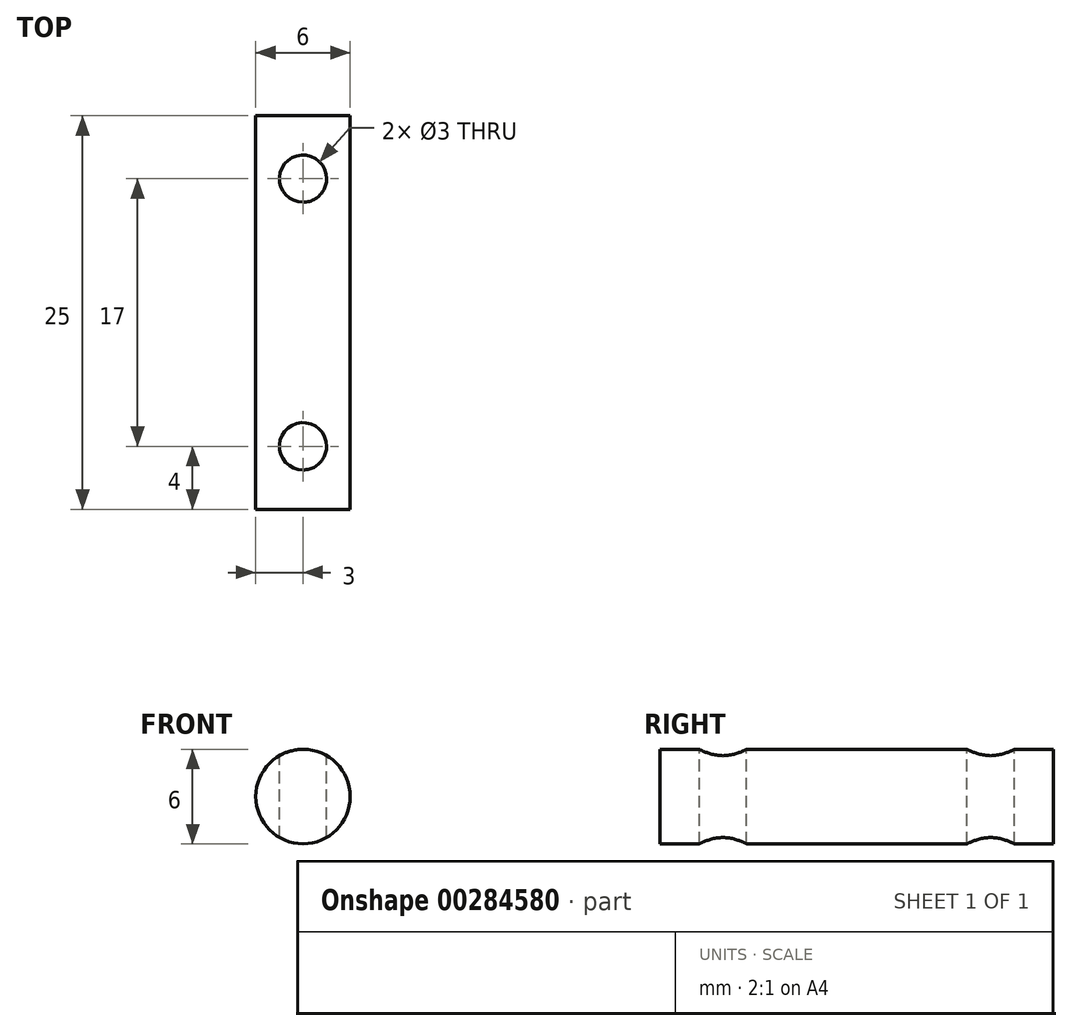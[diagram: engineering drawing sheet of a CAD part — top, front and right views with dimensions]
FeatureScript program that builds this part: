
annotation { "Feature Type Name" : "Feature", "Feature Type Description" : "" }
export const myFeature = defineFeature(function(context is Context, id is Id, definition is map)
    precondition{}
    {
        {
            var Q0;
            Q0=qCreatedBy(makeId("Front.planeOp"),FACE);
            var sketch = newSketch(context, id + "F0", { "sketchPlane" : qUnion([Q0])});
            skCircle(sketch, "E0", {"center": v(0, 0) * mm, "radius": 3 * mm});
            skSolve(sketch);
        }
        {
            var Q0;
            Q0=makeQuery(id+"F0.imprint","IMPRINT",FACE,{"disambiguationData":[TD([[makeQuery(id+"F0.imprint","IMPRINT",EDGE,{"derivedFrom":sQuery(id+"F0.wireOp",EDGE,"E0")}),1.0]])]});
            extrude(context, id + "F1", {"entities" : qUnion([Q0]), "depth" : 25 * mm});
        }
        {
            var Q0;
            Q0=qCreatedBy(makeId("Top.planeOp"),FACE);
            var sketch = newSketch(context, id + "F2", { "sketchPlane" : qUnion([Q0])});
            skPoint(sketch, "E1", {"position": v(0, -21) * mm});
            skPoint(sketch, "E2", {"position": v(0, -4) * mm});
            skPoint(sketch, "E3.start.orphan", {"position": v(0, 0) * mm});
            skCircle(sketch, "E4", {"center": v(0, -4) * mm, "radius": 1.5 * mm});
            skCircle(sketch, "E5", {"center": v(0, -21) * mm, "radius": 1.5 * mm});
            skLineSegment(sketch, "E6", {"start": v(0, -4) * mm, "end": v(0, -21) * mm, "construction": true});
            skLineSegment(sketch, "E7", {"start": v(0, -4) * mm, "end": v(0, 0) * mm, "construction": true});
            skLineSegment(sketch, "E8.0", {"start": v(3, -25) * mm, "end": v(-3, -25) * mm});
            skLineSegment(sketch, "E9", {"start": v(0, -21) * mm, "end": v(0, -25) * mm, "construction": true});
            skSolve(sketch);
        }
        {
            var Q0;
            Q0=qSketchRegion(id+"F2",true);
            extrude(context, id + "F3", {"entities" : qUnion([Q0]), "operationType" : NewBodyOperationType.REMOVE, "endBound" : BoundingType.SYMMETRIC, "oppositeDirection" : true, "depth" : 10 * mm});
        }
    });
